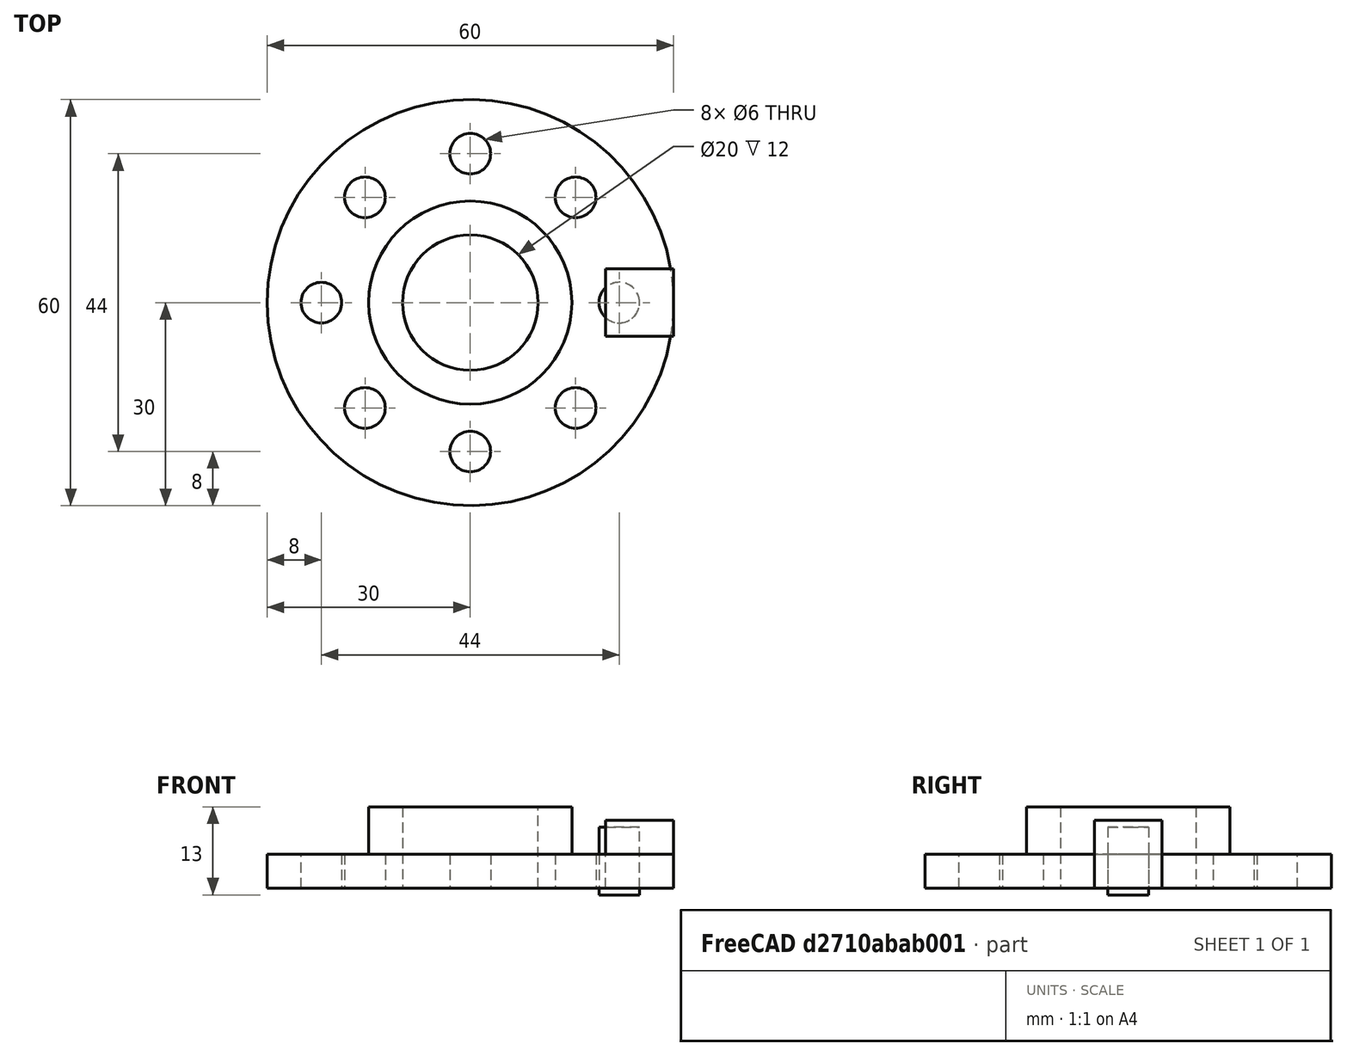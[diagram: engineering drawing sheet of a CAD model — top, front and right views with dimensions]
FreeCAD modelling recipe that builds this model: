
FCSTD DOCUMENT  (FreeCAD 1.0R39319 (Git))
Label: ojt1_t11p01_flange
License: All rights reserved
LicenseURL: https://en.wikipedia.org/wiki/All_rights_reserved
objects: Part::Cylinder×4, Part::Cut×2, Part::Box×1, Part::MultiFuse×1, Part::FeaturePython×1
note: 8 computed .brp shape members not serialized (recipe doc carries the construction recipe); baked Part::Feature solids carry a one-line shape summary decoded from their .brp

FEATURE [Part::Box] Box  label="Cub"
  AttacherType = Attacher::AttachEngine3D
  Height = 10
  Length = 10
  Placement = pos=(20,-5,0) rot=(0,0,1;0rad)
  Width = 10
FEATURE [Part::Cylinder] Cylinder  label="Base"
  Angle = 360
  AttacherType = Attacher::AttachEngine3D
  FirstAngle = 0
  Height = 5
  Radius = 30
  SecondAngle = 0
FEATURE [Part::Cylinder] Cylinder001  label="tub exterior"
  Angle = 360
  AttacherType = Attacher::AttachEngine3D
  FirstAngle = 0
  Height = 12
  Radius = 15
  SecondAngle = 0
FEATURE [Part::MultiFuse] Fusion
  Shapes = -> [Cylinder,Cylinder001]
FEATURE [Part::Cylinder] Cylinder002  label="tub interior"
  Angle = 360
  AttacherType = Attacher::AttachEngine3D
  FirstAngle = 0
  Height = 30
  Placement = pos=(0,0,-1) rot=(0,0,1;0rad)
  Radius = 10
  SecondAngle = 0
FEATURE [Part::Cut] Cut  label="brida sense taladros"
  Base = -> Fusion
  Tool = -> Cylinder002
FEATURE [Part::Cylinder] Cylinder003  label="taladro master"
  Angle = 360
  AttacherType = Attacher::AttachEngine3D
  FirstAngle = 0
  Height = 10
  Placement = pos=(22,0,-1) rot=(0,0,1;0rad)
  Radius = 3
  SecondAngle = 0
FEATURE [Part::FeaturePython] Array  # Draft array (typed FeaturePython)
  AlwaysSyncPlacement = false
  Angle = 360
  ArrayType = 1
  Axis = (0,0,1)
  Base = -> Cylinder003
  Center = (0,0,0)
  Count = 8
  ExpandArray = false
  Fuse = false
  IntervalAxis = (0,0,0)
  IntervalX = (100,0,0)
  IntervalY = (0,100,0)
  IntervalZ = (0,0,100)
  NumberCircles = 3
  NumberPolar = 8
  NumberX = 2
  NumberY = 2
  NumberZ = 1
  PlacementList = 8 placements: [(22,0,-1),(15.5563,15.5563,-1),(0,22,-1),(-15.5563,15.5563,-1),(-22,2.69422e-15,-1),(-15.5563,-15.5563,-1),(-4.88498e-15,-22,-1),(15.5563,-15.5563,-1)]
  RadialDistance = 50
  ScaleList = (8) [(1,1,1),(1,1,1),(1,1,1),(1,1,1),(1,1,1),(1,1,1),(1,1,1),(1,1,1)]
  Symmetry = 1
  TangentialDistance = 25
FEATURE [Part::Cut] Cut001
  Base = -> Cut
  Tool = -> Array
